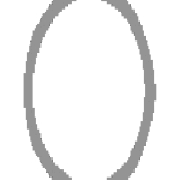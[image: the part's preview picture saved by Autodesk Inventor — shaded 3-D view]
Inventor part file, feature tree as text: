
AUTODESK INVENTOR PART (.ipt)
format: ipt  version: 2021 (Build 250183000, 183)  size: 109,056 bytes
history: native  units: in
note: dims shown in document units (in); Inventor stores cm internally (conversion verified against a paired STEP export)
features: other x4, sketch x3, plane x1
ambient origin geometry x8: Origin, YZ Plane, XZ Plane, XY Plane, X Axis, Y Axis, Z Axis, Center Point
bodies: Solid1 (feature_tree), Body (feature_tree)
feature tree (8):
  other  "Driven Length"
  other  "Frame Generator"
  other  "Start Plane"
  other  "End Plane"
  sketch  "Sketch"  dims[d2=22.3842in d4=-0.0in d5=22.3842in d6=0.12in d7=0.0in d8=90.0deg d9=22.3842in]
  sketch  "Sketch2"  dims[d0=1.0in]
  plane  "Work Plane3"
  sketch  "Sketch3"  dims[d1=0.065in]
